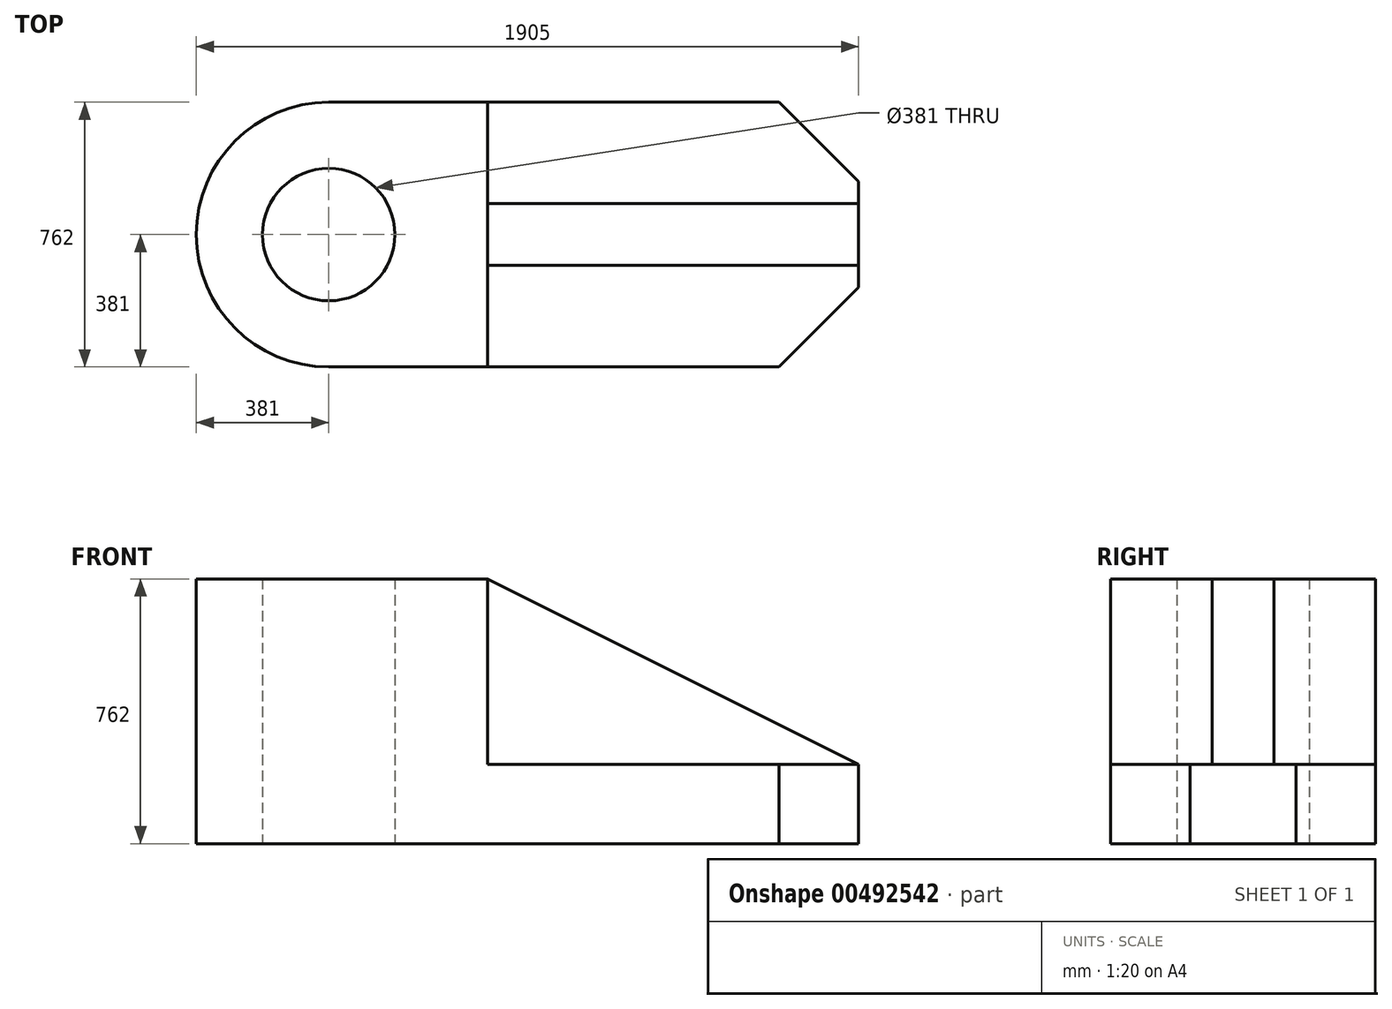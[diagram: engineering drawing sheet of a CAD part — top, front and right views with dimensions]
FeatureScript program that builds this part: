
annotation { "Feature Type Name" : "Feature", "Feature Type Description" : "" }
export const myFeature = defineFeature(function(context is Context, id is Id, definition is map)
    precondition{}
    {
        {
            var Q0;
            Q0=qCreatedBy(makeId("Top.planeOp"),FACE);
            var sketch = newSketch(context, id + "F0", { "sketchPlane" : qUnion([Q0])});
            skLineSegment(sketch, "E0.bottom", {"start": v(0, 0) * mm, "end": v(1905, 0) * mm});
            skLineSegment(sketch, "E0.top", {"start": v(0, 762) * mm, "end": v(1905, 762) * mm});
            skLineSegment(sketch, "E0.left", {"start": v(0, 0) * mm, "end": v(0, 762) * mm});
            skLineSegment(sketch, "E0.right", {"start": v(1905, 0) * mm, "end": v(1905, 762) * mm});
            skCircle(sketch, "E1", {"center": v(381, 381) * mm, "radius": 381 * mm});
            skPoint(sketch, "E1.centerSnap0", {"position": v(0, 381) * mm});
            skLineSegment(sketch, "E2", {"start": v(1676.4, 762) * mm, "end": v(1905, 533.4) * mm});
            skLineSegment(sketch, "E3", {"start": v(1905, 228.6) * mm, "end": v(1676.4, 0) * mm});
            skCircle(sketch, "E4", {"center": v(381, 381) * mm, "radius": 190.5 * mm});
            skSolve(sketch);
        }
        {
            var Q0;
            {var subQ5=sQuery(id+"F0.wireOp",EDGE,"E2");Q0=makeQuery(id+"F0.imprint","IMPRINT",FACE,{"disambiguationData":[TD([[makeQuery(id+"F0.imprint","IMPRINT",EDGE,{"derivedFrom":subQ5}),-1.0]])]});}
            var Q1;
            {var subQ0=sQuery(id+"F0.wireOp",EDGE,"E1");var subQ1=makeQuery(id+"F0.imprint","INTERSECT",VERTEX,{"derivedFrom":[sQuery(id+"F0.wireOp",EDGE,"E0.top"),subQ0]});Q1=makeQuery(id+"F0.imprint","IMPRINT",FACE,{"disambiguationData":[TD([[makeQuery(id+"F0.imprint","IMPRINT",EDGE,{"disambiguationData":[TD([[subQ1,-1.0]])],"derivedFrom":subQ0}),1.0]])]});}
            extrude(context, id + "F1", {"entities" : qUnion([Q0, Q1]), "offsetDistance" : 25.4 * mm, "depth" : 228.6 * mm});
        }
        {
            var Q0;
            Q0=makeQuery(id+"F1.opExtrude","CAP_FACE",FACE,{"disambiguationData":[OSD([sQuery(id+"F0.wireOp",EDGE,"E0.bottom"),sQuery(id+"F0.wireOp",EDGE,"E0.top"),sQuery(id+"F0.wireOp",EDGE,"E0.right"),sQuery(id+"F0.wireOp",EDGE,"E1"),sQuery(id+"F0.wireOp",EDGE,"E2"),sQuery(id+"F0.wireOp",EDGE,"E3")])],"isStart":false});
            var sketch = newSketch(context, id + "F2", { "sketchPlane" : qUnion([Q0])});
            skLineSegment(sketch, "E5", {"start": v(838.2, 762) * mm, "end": v(838.2, 0) * mm});
            skArc(sketch, "E6.0", {"start": v(381, 762) * mm, "mid": v(0, 381) * mm, "end": v(381, 0) * mm});
            skLineSegment(sketch, "E7.0", {"start": v(381, 762) * mm, "end": v(838.2, 762) * mm});
            skLineSegment(sketch, "E8.0", {"start": v(381, 0) * mm, "end": v(838.2, 0) * mm});
            skCircle(sketch, "E9.0", {"center": v(381, 381) * mm, "radius": 190.5 * mm});
            skPoint(sketch, "E10.orphan", {"position": v(1905, 762) * mm});
            skPoint(sketch, "E11.orphan", {"position": v(1905, 0) * mm});
            skPoint(sketch, "E12.orphan", {"position": v(0, 0) * mm});
            skPoint(sketch, "E13.orphan", {"position": v(0, 762) * mm});
            skSolve(sketch);
        }
        {
            var Q0;
            {var subQ0=sQuery(id+"F2.wireOp",EDGE,"E5");Q0=makeQuery(id+"F2.imprint","IMPRINT",FACE,{"disambiguationData":[TD([[makeQuery(id+"F2.imprint","IMPRINT",EDGE,{"derivedFrom":subQ0}),-1.0]])]});}
            extrude(context, id + "F3", {"entities" : qUnion([Q0]), "operationType" : NewBodyOperationType.ADD, "offsetDistance" : 25.4 * mm, "depth" : 533.4 * mm});
        }
        {
            var Q0;
            {var subQ0=sQuery(id+"F0.wireOp",EDGE,"E0.bottom");Q0=makeQuery(id+"F3.boolean.opBoolean","MERGE",FACE,{"derivedFrom":[makeQuery(id+"F1.opExtrude","SWEPT_FACE",FACE,{"disambiguationData":[OSD([subQ0])]}),makeQuery(id+"F3.opExtrude","SWEPT_FACE",FACE,{"disambiguationData":[OSD([subQ0])]})]});}
            var Q1;
            {var subQ0=sQuery(id+"F0.wireOp",EDGE,"E0.top");Q1=makeQuery(id+"F3.boolean.opBoolean","MERGE",FACE,{"derivedFrom":[makeQuery(id+"F1.opExtrude","SWEPT_FACE",FACE,{"disambiguationData":[OSD([subQ0])]}),makeQuery(id+"F3.opExtrude","SWEPT_FACE",FACE,{"disambiguationData":[OSD([subQ0])]})]});}
            cPlane(context, id + "F4", {"entities" : qUnion([Q0, Q1]), "cplaneType" : CPlaneType.MID_PLANE, "offset" : 25.4 * mm, "width" : 152.4 * mm, "height" : 152.4 * mm});
        }
        {
            var Q0;
            Q0=qCreatedBy(id+"F4.planeOp",FACE);
            var sketch = newSketch(context, id + "F5", { "sketchPlane" : qUnion([Q0])});
            skLineSegment(sketch, "E14.0.1", {"start": v(1905, 0) * mm, "end": v(1905, 228.6) * mm});
            skLineSegment(sketch, "E14.0.3", {"start": v(1905, 228.6) * mm, "end": v(1905, 0) * mm});
            skLineSegment(sketch, "E15.0.1", {"start": v(838.2, 228.6) * mm, "end": v(838.2, 762) * mm});
            skLineSegment(sketch, "E15.0.3", {"start": v(838.2, 762) * mm, "end": v(838.2, 228.6) * mm});
            skLineSegment(sketch, "E16", {"start": v(1905, 228.6) * mm, "end": v(838.2, 762) * mm});
            skLineSegment(sketch, "E17.0.0", {"start": v(1676.4, 228.6) * mm, "end": v(838.2, 228.6) * mm});
            skLineSegment(sketch, "E17.0.2", {"start": v(838.2, 228.6) * mm, "end": v(1676.4, 228.6) * mm});
            skLineSegment(sketch, "E17.0.3", {"start": v(1676.4, 228.6) * mm, "end": v(1905, 228.6) * mm});
            skLineSegment(sketch, "E17.0.5", {"start": v(1905, 228.6) * mm, "end": v(1676.4, 228.6) * mm});
            skSolve(sketch);
        }
        {
            var Q0;
            Q0 = qSketchRegion(id + "F5", true);
            extrude(context, id + "F6", {"entities" : qUnion([Q0]), "operationType" : NewBodyOperationType.ADD, "offsetDistance" : 25.4 * mm, "depth" : 177.8 * mm, "symmetric" : true});
        }
    });
